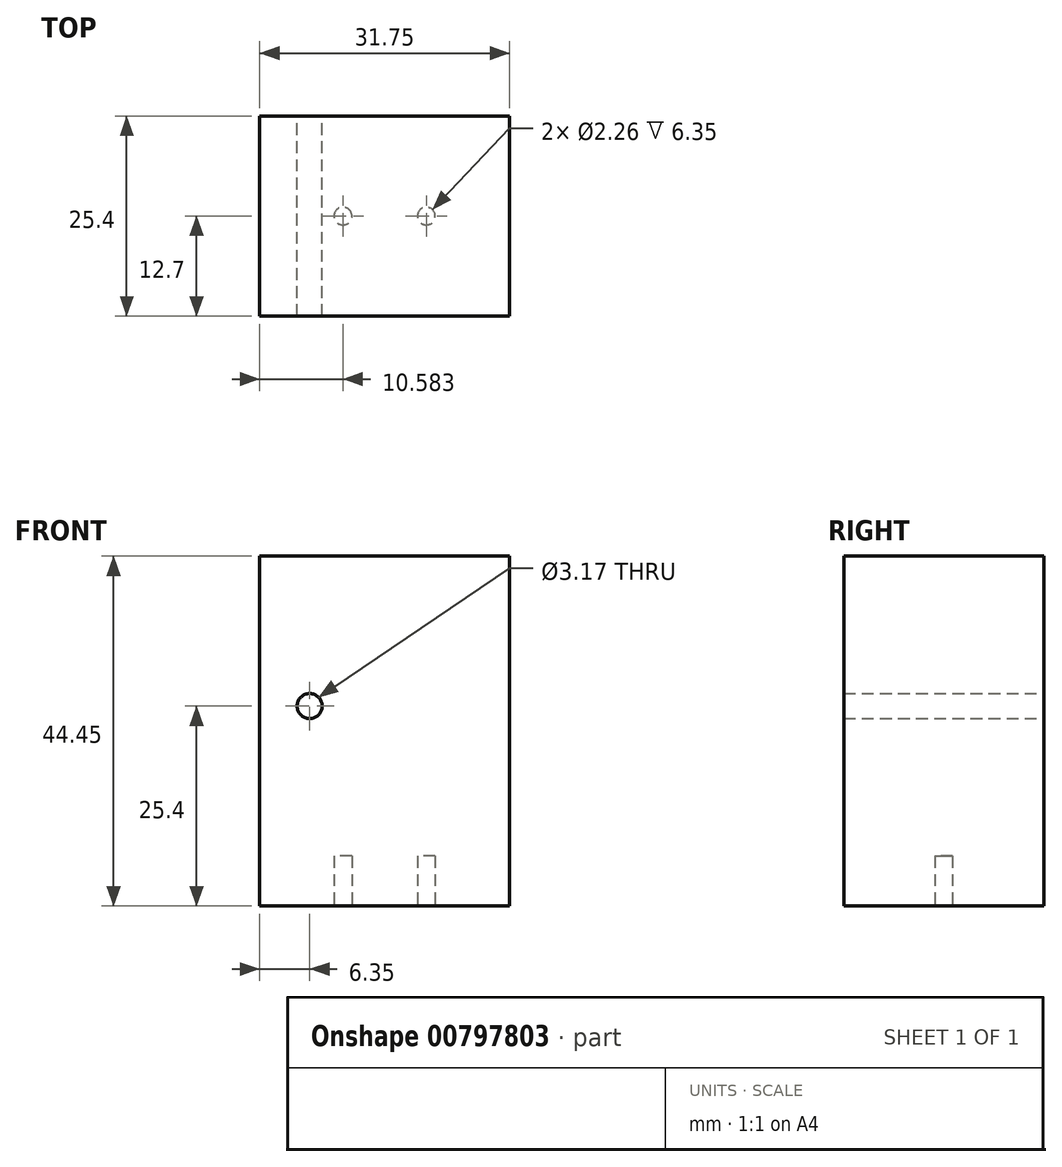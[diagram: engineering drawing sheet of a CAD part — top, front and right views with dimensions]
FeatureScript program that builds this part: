
annotation { "Feature Type Name" : "Feature", "Feature Type Description" : "" }
export const myFeature = defineFeature(function(context is Context, id is Id, definition is map)
    precondition{}
    {
        {
            var Q0;
            Q0=qCreatedBy(makeId("Front.planeOp"),FACE);
            var sketch = newSketch(context, id + "F0", { "sketchPlane" : qUnion([Q0])});
            skLineSegment(sketch, "E0.bottom", {"start": v(-31.75, 44.45) * mm, "end": v(0, 44.45) * mm});
            skLineSegment(sketch, "E0.top", {"start": v(-31.75, 0) * mm, "end": v(0, 0) * mm});
            skLineSegment(sketch, "E0.left", {"start": v(-31.75, 44.45) * mm, "end": v(-31.75, 0) * mm});
            skLineSegment(sketch, "E0.right", {"start": v(0, 44.45) * mm, "end": v(0, 0) * mm});
            skCircle(sketch, "E1", {"center": v(-25.4, 25.4) * mm, "radius": 1.59 * mm});
            skCircle(sketch, "E2", {"center": v(6.35, 25.4) * mm, "radius": 1.59 * mm});
            skLineSegment(sketch, "E3", {"start": v(-25.4, 25.4) * mm, "end": v(-25.4, 0) * mm, "construction": true});
            skLineSegment(sketch, "E4", {"start": v(6.35, 25.4) * mm, "end": v(6.35, 0) * mm, "construction": true});
            skLineSegment(sketch, "E5", {"start": v(-25.4, 25.4) * mm, "end": v(6.35, 25.4) * mm, "construction": true});
            skLineSegment(sketch, "E6", {"start": v(0, 25.4) * mm, "end": v(6.35, 25.4) * mm, "construction": true});
            skLineSegment(sketch, "E7", {"start": v(-25.4, 25.4) * mm, "end": v(-31.75, 25.4) * mm, "construction": true});
            skSolve(sketch);
        }
        {
            var Q0;
            Q0=makeQuery(id+"F0.imprint","IMPRINT",FACE,{"disambiguationData":[TD([[makeQuery(id+"F0.imprint","IMPRINT",EDGE,{"derivedFrom":sQuery(id+"F0.wireOp",EDGE,"E0.bottom")}),-1.0]])]});
            var Q1;
            Q1=sQuery(id+"F0.wireOp",EDGE,"E0.right");
            var Q2;
            Q2=sQuery(id+"F0.wireOp",EDGE,"E0.top");
            var Q3;
            Q3=sQuery(id+"F0.wireOp",EDGE,"E0.left");
            extrude(context, id + "F1", {"entities" : qUnion([Q0]), "surfaceEntities" : qUnion([Q1, Q2, Q3]), "depth" : 25.4 * mm, "offsetDistance" : 25.4 * mm});
        }
        {
            var Q0;
            Q0=qCreatedBy(makeId("Top.planeOp"),FACE);
            var sketch = newSketch(context, id + "F2", { "sketchPlane" : qUnion([Q0])});
            skCircle(sketch, "E8", {"center": v(-21.17, -12.7) * mm, "radius": 1.13 * mm});
            skCircle(sketch, "E9", {"center": v(-10.58, -12.7) * mm, "radius": 1.13 * mm});
            skLineSegment(sketch, "E10", {"start": v(-31.75, -12.7) * mm, "end": v(-21.17, -12.7) * mm, "construction": true});
            skLineSegment(sketch, "E11", {"start": v(-21.17, -12.7) * mm, "end": v(-10.58, -12.7) * mm, "construction": true});
            skLineSegment(sketch, "E12", {"start": v(-10.58, -12.7) * mm, "end": v(0, -12.7) * mm, "construction": true});
            skSolve(sketch);
        }
        {
            var Q0;
            {var subQ0=sQuery(id+"F2.wireOp",EDGE,"E10");var subQ1=sQuery(id+"F2.wireOp",EDGE,"E8");var subQ2=makeQuery(id+"F2.imprint","INTERSECT",VERTEX,{"derivedFrom":[subQ1,subQ0]});Q0=makeQuery(id+"F2.imprint","IMPRINT",FACE,{"disambiguationData":[TD([[makeQuery(id+"F2.imprint","IMPRINT",EDGE,{"disambiguationData":[TD([[subQ2,-1.0]])],"derivedFrom":subQ1}),1.0]])]});}
            var Q1;
            {var subQ0=sQuery(id+"F2.wireOp",EDGE,"E10");var subQ1=sQuery(id+"F2.wireOp",EDGE,"E8");var subQ2=makeQuery(id+"F2.imprint","INTERSECT",VERTEX,{"derivedFrom":[subQ1,subQ0]});Q1=makeQuery(id+"F2.imprint","IMPRINT",FACE,{"disambiguationData":[TD([[makeQuery(id+"F2.imprint","IMPRINT",EDGE,{"disambiguationData":[TD([[subQ2,1.0]])],"derivedFrom":subQ1}),1.0]])]});}
            var Q2;
            {var subQ0=sQuery(id+"F2.wireOp",EDGE,"E11");var subQ1=sQuery(id+"F2.wireOp",EDGE,"E9");var subQ2=makeQuery(id+"F2.imprint","INTERSECT",VERTEX,{"derivedFrom":[subQ1,subQ0]});Q2=makeQuery(id+"F2.imprint","IMPRINT",FACE,{"disambiguationData":[TD([[makeQuery(id+"F2.imprint","IMPRINT",EDGE,{"disambiguationData":[TD([[subQ2,-1.0]])],"derivedFrom":subQ1}),1.0]])]});}
            var Q3;
            {var subQ0=sQuery(id+"F2.wireOp",EDGE,"E11");var subQ1=sQuery(id+"F2.wireOp",EDGE,"E9");var subQ2=makeQuery(id+"F2.imprint","INTERSECT",VERTEX,{"derivedFrom":[subQ1,subQ0]});Q3=makeQuery(id+"F2.imprint","IMPRINT",FACE,{"disambiguationData":[TD([[makeQuery(id+"F2.imprint","IMPRINT",EDGE,{"disambiguationData":[TD([[subQ2,1.0]])],"derivedFrom":subQ1}),1.0]])]});}
            extrude(context, id + "F3", {"entities" : qUnion([Q0, Q1, Q2, Q3]), "operationType" : NewBodyOperationType.REMOVE, "depth" : 6.35 * mm, "offsetDistance" : 25.4 * mm});
        }
    });
